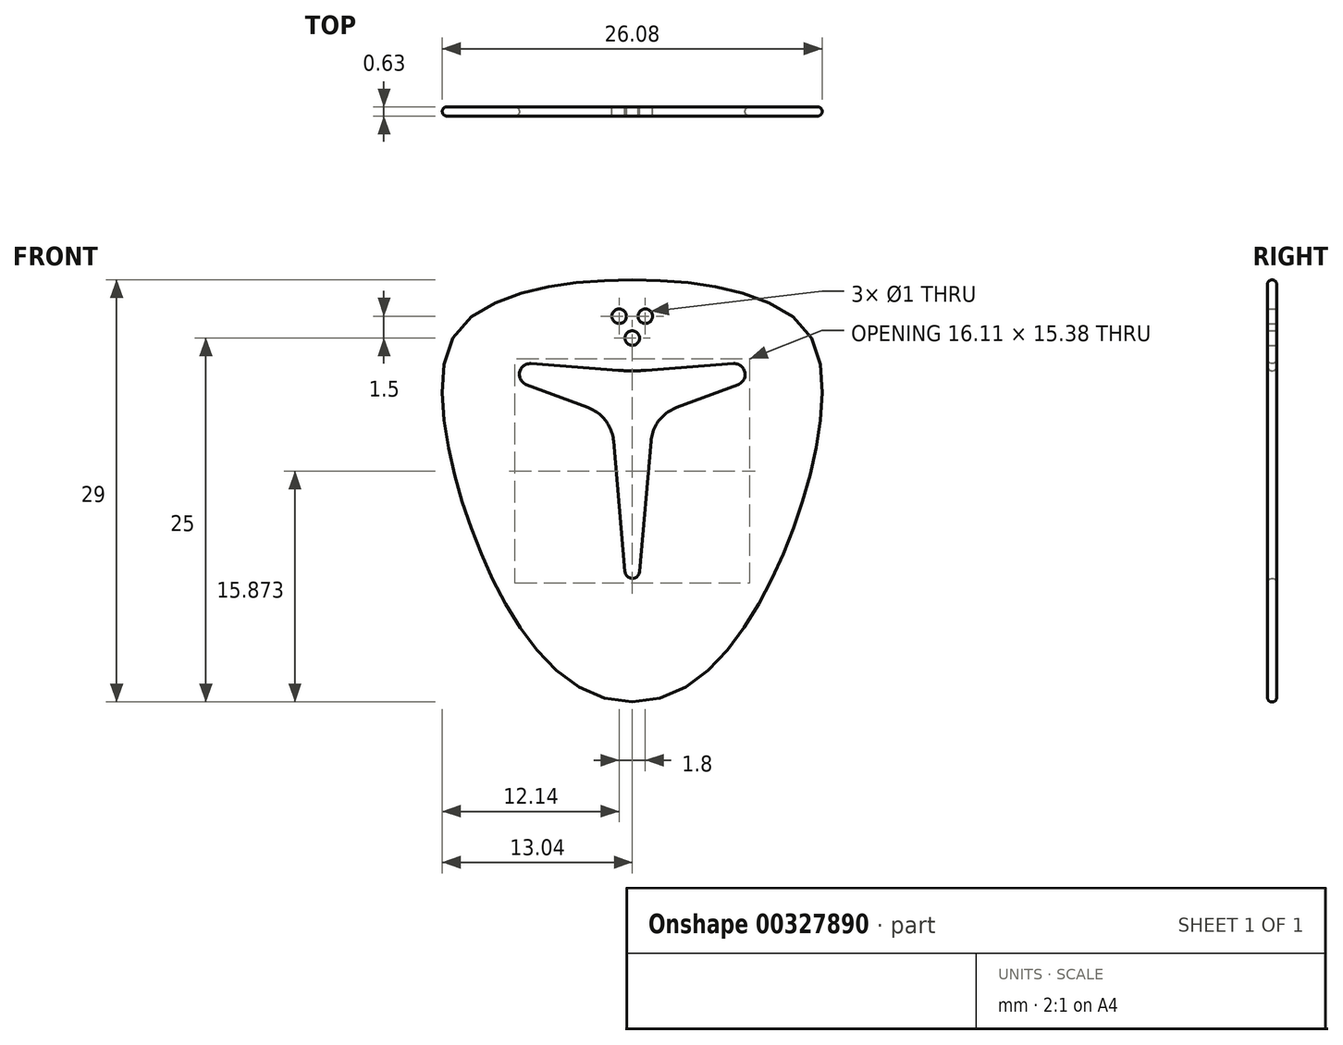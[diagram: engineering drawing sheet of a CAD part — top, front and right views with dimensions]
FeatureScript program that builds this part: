
annotation { "Feature Type Name" : "Feature", "Feature Type Description" : "" }
export const myFeature = defineFeature(function(context is Context, id is Id, definition is map)
    precondition{}
    {
        {
            var Q0;
            Q0=qCreatedBy(makeId("Front.planeOp"),FACE);
            var sketch = newSketch(context, id + "F0", { "sketchPlane" : qUnion([Q0])});
            skLineSegment(sketch, "E0", {"start": v(0, 0) * mm, "end": v(0, 6.5) * mm, "construction": true});
            skLineSegment(sketch, "E1", {"start": v(0, 0) * mm, "end": v(0, -22.5) * mm, "construction": true});
            skLineSegment(sketch, "E2", {"start": v(0, 0) * mm, "end": v(13, 0) * mm, "construction": true});
            skFitSpline(sketch, "E3", {"points": [v(0, -22.5) * mm, v(10.5, -12) * mm, v(13, 0) * mm, v(11, 4) * mm, v(0, 6.5) * mm], "startDerivative": vector(49.93, 0) * mm, "endDerivative": vector(-57.3, 0) * mm});
            skFitSpline(sketch, "E4.MirrorCS", {"points": [v(0, -22.5) * mm, v(-10.5, -12) * mm, v(-13, 0) * mm, v(-11, 4) * mm, v(0, 6.5) * mm], "startDerivative": vector(-49.93, 0) * mm, "endDerivative": vector(57.3, 0) * mm});
            skArc(sketch, "E5", {"start": v(7.26, -0.7) * mm, "mid": v(7.73, 0.16) * mm, "end": v(6.94, 0.75) * mm});
            skLineSegment(sketch, "E6", {"start": v(7.26, -0.7) * mm, "end": v(3.04, -2.27) * mm});
            skArc(sketch, "E7", {"start": v(3.04, -2.27) * mm, "mid": v(1.83, -3.17) * mm, "end": v(1.28, -4.58) * mm});
            skLineSegment(sketch, "E8", {"start": v(0.5, -13.54) * mm, "end": v(1.28, -4.58) * mm});
            skArc(sketch, "E9", {"start": v(0, -14) * mm, "mid": v(0.34, -13.87) * mm, "end": v(0.5, -13.54) * mm});
            skArc(sketch, "E10.MirrorCS", {"start": v(0, -14) * mm, "mid": v(-0.34, -13.87) * mm, "end": v(-0.5, -13.54) * mm});
            skLineSegment(sketch, "E11.MirrorCS", {"start": v(-0.5, -13.54) * mm, "end": v(-1.28, -4.58) * mm});
            skArc(sketch, "E12.MirrorCS", {"start": v(-3.04, -2.27) * mm, "mid": v(-1.83, -3.17) * mm, "end": v(-1.28, -4.58) * mm});
            skLineSegment(sketch, "E13.MirrorCS", {"start": v(-7.26, -0.7) * mm, "end": v(-3.04, -2.27) * mm});
            skArc(sketch, "E14.MirrorCS", {"start": v(-7.26, -0.7) * mm, "mid": v(-7.73, 0.16) * mm, "end": v(-6.94, 0.75) * mm});
            skLineSegment(sketch, "E15", {"start": v(6.94, 0.75) * mm, "end": v(0.96, 0.29) * mm});
            skArc(sketch, "E16", {"start": v(0, 0.25) * mm, "mid": v(0.48, 0.26) * mm, "end": v(0.96, 0.29) * mm});
            skArc(sketch, "E17.MirrorCS", {"start": v(0, 0.25) * mm, "mid": v(-0.48, 0.26) * mm, "end": v(-0.96, 0.29) * mm});
            skLineSegment(sketch, "E18.MirrorCS", {"start": v(-6.94, 0.75) * mm, "end": v(-0.96, 0.29) * mm});
            skCircle(sketch, "E19", {"center": v(0, 2.5) * mm, "radius": 0.5 * mm});
            skCircle(sketch, "E20", {"center": v(0.9, 4) * mm, "radius": 0.5 * mm});
            skLineSegment(sketch, "E21", {"start": v(0.9, 4) * mm, "end": v(0, 4) * mm});
            skPoint(sketch, "E22", {"position": v(0, 3.25) * mm});
            skLineSegment(sketch, "E23.MirrorCS", {"start": v(-0.9, 4) * mm, "end": v(0, 4) * mm});
            skCircle(sketch, "E24.MirrorC", {"center": v(-0.9, 4) * mm, "radius": 0.5 * mm});
            skSolve(sketch);
        }
        {
            var Q0;
            Q0=qSketchRegion(id+"F0",true);
            extrude(context, id + "F1", {"entities" : qUnion([Q0]), "depth" : 0.63 * mm});
        }
        {
            var Q0;
            Q0=makeQuery(id+"F1.opExtrude","CAP_EDGE",EDGE,{"disambiguationData":[OSD([sQuery(id+"F0.wireOp",EDGE,"E5")])],"isStart":false});
            var Q1;
            Q1=makeQuery(id+"F1.opExtrude","CAP_EDGE",EDGE,{"disambiguationData":[OSD([sQuery(id+"F0.wireOp",EDGE,"E7")])],"isStart":true});
            var Q2;
            Q2=makeQuery(id+"F1.opExtrude","CAP_EDGE",EDGE,{"disambiguationData":[OSD([sQuery(id+"F0.wireOp",EDGE,"E9"),sQuery(id+"F0.wireOp",EDGE,"E10.MirrorCS")])],"isStart":false});
            var Q3;
            Q3=makeQuery(id+"F1.opExtrude","CAP_EDGE",EDGE,{"disambiguationData":[OSD([sQuery(id+"F0.wireOp",EDGE,"E14.MirrorCS")])],"isStart":false});
            var Q4;
            Q4=makeQuery(id+"F1.opExtrude","CAP_EDGE",EDGE,{"disambiguationData":[OSD([sQuery(id+"F0.wireOp",EDGE,"E5")])],"isStart":true});
            var Q5;
            Q5=makeQuery(id+"F1.opExtrude","CAP_EDGE",EDGE,{"disambiguationData":[OSD([sQuery(id+"F0.wireOp",EDGE,"E12.MirrorCS")])],"isStart":false});
            var Q6;
            Q6=makeQuery(id+"F1.opExtrude","CAP_EDGE",EDGE,{"disambiguationData":[OSD([sQuery(id+"F0.wireOp",EDGE,"E7")])],"isStart":false});
            var Q7;
            Q7=makeQuery(id+"F1.opExtrude","CAP_EDGE",EDGE,{"disambiguationData":[OSD([sQuery(id+"F0.wireOp",EDGE,"cP70XH3B-hxny-nh1n-TbyW-52Zl4TOD4HrO"),sQuery(id+"F0.wireOp",EDGE,"9cf6c757-e815-40dd-95a7-672993b90d513.MirrorCS")])],"isStart":true});
            var Q8;
            Q8=makeQuery(id+"F1.opExtrude","CAP_EDGE",EDGE,{"disambiguationData":[OSD([sQuery(id+"F0.wireOp",EDGE,"E13.MirrorCS")])],"isStart":false});
            var Q9;
            Q9=makeQuery(id+"F1.opExtrude","CAP_EDGE",EDGE,{"disambiguationData":[OSD([sQuery(id+"F0.wireOp",EDGE,"E12.MirrorCS")])],"isStart":true});
            var Q10;
            Q10=makeQuery(id+"F1.opExtrude","CAP_EDGE",EDGE,{"disambiguationData":[OSD([sQuery(id+"F0.wireOp",EDGE,"cP70XH3B-hxny-nh1n-TbyW-52Zl4TOD4HrO"),sQuery(id+"F0.wireOp",EDGE,"9cf6c757-e815-40dd-95a7-672993b90d513.MirrorCS")])],"isStart":false});
            var Q11;
            Q11=makeQuery(id+"F1.opExtrude","CAP_EDGE",EDGE,{"disambiguationData":[OSD([sQuery(id+"F0.wireOp",EDGE,"E9"),sQuery(id+"F0.wireOp",EDGE,"E10.MirrorCS")])],"isStart":true});
            var Q12;
            Q12=makeQuery(id+"F1.opExtrude","SWEPT_EDGE",EDGE,{"disambiguationData":[OSD([sQuery(id+"F0.wireOp",EDGE,"9cf6c757-e815-40dd-95a7-672993b90d513.MirrorCS"),sQuery(id+"F0.wireOp",EDGE,"E14.MirrorCS")])]});
            var Q13;
            Q13=makeQuery(id+"F1.opExtrude","CAP_EDGE",EDGE,{"disambiguationData":[OSD([sQuery(id+"F0.wireOp",EDGE,"E8")])],"isStart":true});
            var Q14;
            Q14=makeQuery(id+"F1.opExtrude","CAP_EDGE",EDGE,{"disambiguationData":[OSD([sQuery(id+"F0.wireOp",EDGE,"E11.MirrorCS")])],"isStart":false});
            var Q15;
            Q15=makeQuery(id+"F1.opExtrude","SWEPT_EDGE",EDGE,{"disambiguationData":[OSD([sQuery(id+"F0.wireOp",EDGE,"E6"),sQuery(id+"F0.wireOp",EDGE,"E7")])]});
            var Q16;
            Q16=makeQuery(id+"F1.opExtrude","SWEPT_EDGE",EDGE,{"disambiguationData":[OSD([sQuery(id+"F0.wireOp",EDGE,"E8"),sQuery(id+"F0.wireOp",EDGE,"E9")])]});
            var Q17;
            Q17=makeQuery(id+"F1.opExtrude","SWEPT_EDGE",EDGE,{"disambiguationData":[OSD([sQuery(id+"F0.wireOp",EDGE,"E13.MirrorCS"),sQuery(id+"F0.wireOp",EDGE,"E14.MirrorCS")])]});
            var Q18;
            Q18=makeQuery(id+"F1.opExtrude","SWEPT_EDGE",EDGE,{"disambiguationData":[OSD([sQuery(id+"F0.wireOp",EDGE,"E10.MirrorCS"),sQuery(id+"F0.wireOp",EDGE,"E11.MirrorCS")])]});
            var Q19;
            Q19=makeQuery(id+"F1.opExtrude","SWEPT_EDGE",EDGE,{"disambiguationData":[OSD([sQuery(id+"F0.wireOp",EDGE,"E11.MirrorCS"),sQuery(id+"F0.wireOp",EDGE,"E12.MirrorCS")])]});
            var Q20;
            Q20=makeQuery(id+"F1.opExtrude","SWEPT_EDGE",EDGE,{"disambiguationData":[OSD([sQuery(id+"F0.wireOp",EDGE,"E5"),sQuery(id+"F0.wireOp",EDGE,"E6")])]});
            var Q21;
            Q21=makeQuery(id+"F1.opExtrude","CAP_EDGE",EDGE,{"disambiguationData":[OSD([sQuery(id+"F0.wireOp",EDGE,"E14.MirrorCS")])],"isStart":true});
            var Q22;
            Q22=makeQuery(id+"F1.opExtrude","SWEPT_EDGE",EDGE,{"disambiguationData":[OSD([sQuery(id+"F0.wireOp",EDGE,"E12.MirrorCS"),sQuery(id+"F0.wireOp",EDGE,"E13.MirrorCS")])]});
            var Q23;
            Q23=makeQuery(id+"F1.opExtrude","CAP_EDGE",EDGE,{"disambiguationData":[OSD([sQuery(id+"F0.wireOp",EDGE,"E8")])],"isStart":false});
            var Q24;
            Q24=makeQuery(id+"F1.opExtrude","SWEPT_EDGE",EDGE,{"disambiguationData":[OSD([sQuery(id+"F0.wireOp",EDGE,"cP70XH3B-hxny-nh1n-TbyW-52Zl4TOD4HrO"),sQuery(id+"F0.wireOp",EDGE,"E5")])]});
            var Q25;
            Q25=makeQuery(id+"F1.opExtrude","CAP_EDGE",EDGE,{"disambiguationData":[OSD([sQuery(id+"F0.wireOp",EDGE,"E6")])],"isStart":false});
            var Q26;
            Q26=makeQuery(id+"F1.opExtrude","CAP_EDGE",EDGE,{"disambiguationData":[OSD([sQuery(id+"F0.wireOp",EDGE,"E11.MirrorCS")])],"isStart":true});
            var Q27;
            Q27=makeQuery(id+"F1.opExtrude","SWEPT_EDGE",EDGE,{"disambiguationData":[OSD([sQuery(id+"F0.wireOp",EDGE,"E7"),sQuery(id+"F0.wireOp",EDGE,"E8")])]});
            var Q28;
            Q28=makeQuery(id+"F1.opExtrude","CAP_EDGE",EDGE,{"disambiguationData":[OSD([sQuery(id+"F0.wireOp",EDGE,"E6")])],"isStart":true});
            var Q29;
            Q29=makeQuery(id+"F1.opExtrude","CAP_EDGE",EDGE,{"disambiguationData":[OSD([sQuery(id+"F0.wireOp",EDGE,"E13.MirrorCS")])],"isStart":true});
            var Q30;
            Q30=makeQuery(id+"F1.opExtrude","CAP_EDGE",EDGE,{"disambiguationData":[OSD([sQuery(id+"F0.wireOp",EDGE,"E18.MirrorCS")])],"isStart":false});
            var Q31;
            Q31=makeQuery(id+"F1.opExtrude","CAP_EDGE",EDGE,{"disambiguationData":[OSD([sQuery(id+"F0.wireOp",EDGE,"E18.MirrorCS")])],"isStart":true});
            var Q32;
            Q32=makeQuery(id+"F1.opExtrude","CAP_EDGE",EDGE,{"disambiguationData":[OSD([sQuery(id+"F0.wireOp",EDGE,"E16"),sQuery(id+"F0.wireOp",EDGE,"E17.MirrorCS")])],"isStart":false});
            var Q33;
            Q33=makeQuery(id+"F1.opExtrude","CAP_EDGE",EDGE,{"disambiguationData":[OSD([sQuery(id+"F0.wireOp",EDGE,"E16"),sQuery(id+"F0.wireOp",EDGE,"E17.MirrorCS")])],"isStart":true});
            var Q34;
            Q34=makeQuery(id+"F1.opExtrude","CAP_EDGE",EDGE,{"disambiguationData":[OSD([sQuery(id+"F0.wireOp",EDGE,"E15")])],"isStart":false});
            fillet(context, id + "F2", {"entities" : qUnion([Q0, Q1, Q2, Q3, Q4, Q5, Q6, Q7, Q8, Q9, Q10, Q11, Q12, Q13, Q14, Q15, Q16, Q17, Q18, Q19, Q20, Q21, Q22, Q23, Q24, Q25, Q26, Q27, Q28, Q29, Q30, Q31, Q32, Q33, Q34]), "radius" : (0.63 / 2) * mm, "tangentPropagation" : true, "allowEdgeOverflow" : false});
        }
        {
            var Q0;
            Q0=makeQuery(id+"F1.opExtrude","CAP_EDGE",EDGE,{"disambiguationData":[OSD([sQuery(id+"F0.wireOp",EDGE,"E4.MirrorCS")])],"isStart":false});
            var Q1;
            Q1=makeQuery(id+"F1.opExtrude","CAP_EDGE",EDGE,{"disambiguationData":[OSD([sQuery(id+"F0.wireOp",EDGE,"E3")])],"isStart":false});
            var Q2;
            Q2=makeQuery(id+"F1.opExtrude","CAP_EDGE",EDGE,{"disambiguationData":[OSD([sQuery(id+"F0.wireOp",EDGE,"E4.MirrorCS")])],"isStart":true});
            var Q3;
            Q3=makeQuery(id+"F1.opExtrude","CAP_EDGE",EDGE,{"disambiguationData":[OSD([sQuery(id+"F0.wireOp",EDGE,"E3")])],"isStart":true});
            fillet(context, id + "F3", {"entities" : qUnion([Q0, Q1, Q2, Q3]), "radius" : 0.63 / 2 * mm, "tangentPropagation" : true, "allowEdgeOverflow" : false});
        }
    });
